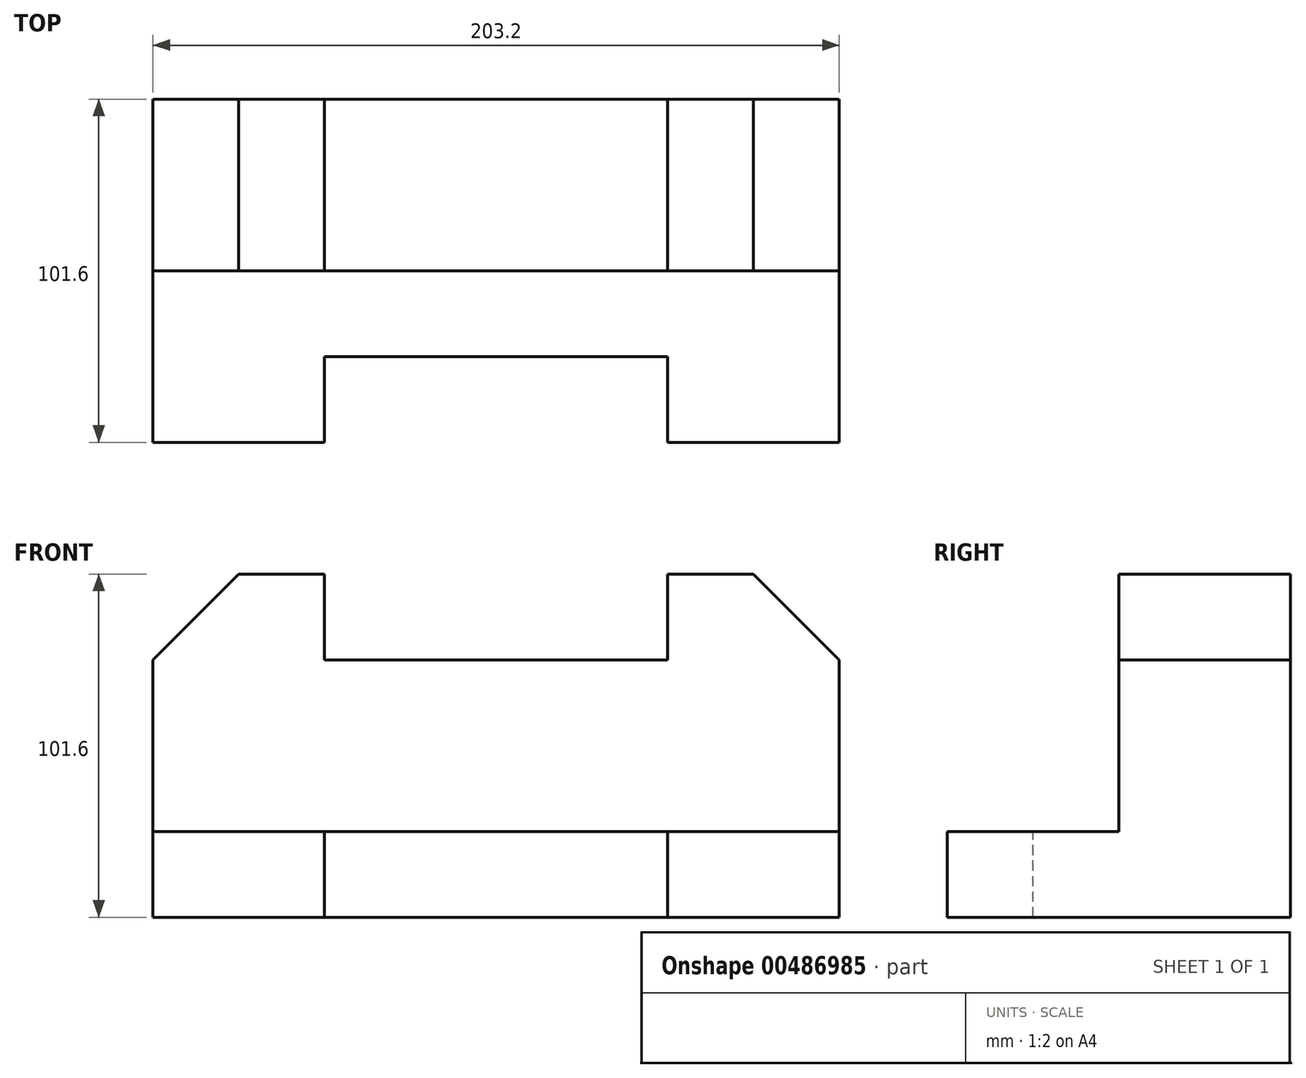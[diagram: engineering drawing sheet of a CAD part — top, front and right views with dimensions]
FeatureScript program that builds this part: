
annotation { "Feature Type Name" : "Feature", "Feature Type Description" : "" }
export const myFeature = defineFeature(function(context is Context, id is Id, definition is map)
    precondition{}
    {
        {
            var Q0;
            Q0=qCreatedBy(makeId("Front.planeOp"),FACE);
            var sketch = newSketch(context, id + "F0", { "sketchPlane" : qUnion([Q0])});
            skLineSegment(sketch, "E0.bottom", {"start": v(-85.33, 57.13) * mm, "end": v(117.87, 57.13) * mm});
            skLineSegment(sketch, "E0.top", {"start": v(-85.33, -44.47) * mm, "end": v(117.87, -44.47) * mm});
            skLineSegment(sketch, "E0.left", {"start": v(-85.33, 57.13) * mm, "end": v(-85.33, -44.47) * mm});
            skLineSegment(sketch, "E0.right", {"start": v(117.87, 57.13) * mm, "end": v(117.87, -44.47) * mm});
            skSolve(sketch);
        }
        {
            var Q0;
            Q0 = qSketchRegion(id + "F0", true);
            extrude(context, id + "F1", {"entities" : qUnion([Q0]), "depth" : 101.6 * mm});
        }
        {
            var Q0;
            Q0=makeQuery(id+"F1.opExtrude","CAP_FACE",FACE,{"disambiguationData":[OSD([sQuery(id+"F0.wireOp",EDGE,"E0.bottom"),sQuery(id+"F0.wireOp",EDGE,"E0.top"),sQuery(id+"F0.wireOp",EDGE,"E0.left"),sQuery(id+"F0.wireOp",EDGE,"E0.right")])],"isStart":false});
            var sketch = newSketch(context, id + "F2", { "sketchPlane" : qUnion([Q0])});
            skLineSegment(sketch, "E1", {"start": v(117.87, -44.47) * mm, "end": v(117.87, -19.07) * mm});
            skLineSegment(sketch, "E2", {"start": v(117.87, -19.07) * mm, "end": v(117.87, 57.13) * mm});
            skLineSegment(sketch, "E3", {"start": v(117.87, 57.13) * mm, "end": v(-85.33, 57.13) * mm});
            skLineSegment(sketch, "E4", {"start": v(-85.33, 57.13) * mm, "end": v(-85.33, -19.07) * mm});
            skLineSegment(sketch, "E5", {"start": v(-85.33, -19.07) * mm, "end": v(117.87, -19.07) * mm});
            skSolve(sketch);
        }
        {
            var Q0;
            Q0 = qSketchRegion(id + "F2", true);
            extrude(context, id + "F3", {"entities" : qUnion([Q0]), "operationType" : NewBodyOperationType.REMOVE, "oppositeDirection" : true, "depth" : 50.8 * mm});
        }
        {
            var Q0;
            Q0=makeQuery(id+"F1.opExtrude","CAP_FACE",FACE,{"disambiguationData":[OSD([sQuery(id+"F0.wireOp",EDGE,"E0.bottom"),sQuery(id+"F0.wireOp",EDGE,"E0.top"),sQuery(id+"F0.wireOp",EDGE,"E0.left"),sQuery(id+"F0.wireOp",EDGE,"E0.right")])],"isStart":false});
            var sketch = newSketch(context, id + "F4", { "sketchPlane" : qUnion([Q0])});
            skLineSegment(sketch, "E6", {"start": v(-85.33, -44.47) * mm, "end": v(-34.53, -44.47) * mm});
            skLineSegment(sketch, "E7", {"start": v(-34.53, -44.47) * mm, "end": v(67.07, -44.47) * mm});
            skLineSegment(sketch, "E8", {"start": v(67.07, -44.47) * mm, "end": v(117.87, -44.47) * mm});
            skLineSegment(sketch, "E9", {"start": v(67.07, -44.47) * mm, "end": v(67.07, -19.07) * mm});
            skLineSegment(sketch, "E10", {"start": v(67.07, -19.07) * mm, "end": v(-34.53, -19.07) * mm});
            skLineSegment(sketch, "E11", {"start": v(-34.53, -19.07) * mm, "end": v(-34.53, -44.47) * mm});
            skSolve(sketch);
        }
        {
            var Q0;
            Q0=makeQuery(id+"F4.imprint","IMPRINT",FACE,{"disambiguationData":[TD([[makeQuery(id+"F4.imprint","IMPRINT",EDGE,{"derivedFrom":sQuery(id+"F4.wireOp",EDGE,"E7")}),1.0]])]});
            extrude(context, id + "F5", {"entities" : qUnion([Q0]), "operationType" : NewBodyOperationType.REMOVE, "oppositeDirection" : true, "depth" : 25.4 * mm});
        }
        {
            var Q0;
            Q0=makeQuery(id+"F3.boolean.opBoolean","COPY",FACE,{"derivedFrom":makeQuery(id+"F3.opExtrude","CAP_FACE",FACE,{"disambiguationData":[OSD([sQuery(id+"F2.wireOp",EDGE,"E2"),sQuery(id+"F2.wireOp",EDGE,"E3"),sQuery(id+"F2.wireOp",EDGE,"E4"),sQuery(id+"F2.wireOp",EDGE,"E5")])],"isStart":false})});
            var sketch = newSketch(context, id + "F6", { "sketchPlane" : qUnion([Q0])});
            skLineSegment(sketch, "E12", {"start": v(-85.33, 57.13) * mm, "end": v(-34.53, 57.13) * mm});
            skLineSegment(sketch, "E13", {"start": v(-34.53, 57.13) * mm, "end": v(67.07, 57.13) * mm});
            skLineSegment(sketch, "E14", {"start": v(67.07, 57.13) * mm, "end": v(117.87, 57.13) * mm});
            skLineSegment(sketch, "E15", {"start": v(-34.53, 57.13) * mm, "end": v(-34.53, 31.73) * mm});
            skLineSegment(sketch, "E16", {"start": v(-34.53, 31.73) * mm, "end": v(67.07, 31.73) * mm});
            skLineSegment(sketch, "E17", {"start": v(67.07, 31.73) * mm, "end": v(67.07, 57.13) * mm});
            skSolve(sketch);
        }
        {
            var Q0;
            Q0=makeQuery(id+"F6.imprint","IMPRINT",FACE,{"disambiguationData":[TD([[makeQuery(id+"F6.imprint","IMPRINT",EDGE,{"derivedFrom":sQuery(id+"F6.wireOp",EDGE,"E13")}),-1.0]])]});
            extrude(context, id + "F7", {"entities" : qUnion([Q0]), "operationType" : NewBodyOperationType.REMOVE, "oppositeDirection" : true, "depth" : 50.8 * mm});
        }
        {
            var Q0;
            Q0=makeQuery(id+"F3.boolean.opBoolean","COPY",FACE,{"derivedFrom":makeQuery(id+"F3.opExtrude","CAP_FACE",FACE,{"disambiguationData":[OSD([sQuery(id+"F2.wireOp",EDGE,"E2"),sQuery(id+"F2.wireOp",EDGE,"E3"),sQuery(id+"F2.wireOp",EDGE,"E4"),sQuery(id+"F2.wireOp",EDGE,"E5")])],"isStart":false})});
            var sketch = newSketch(context, id + "F8", { "sketchPlane" : qUnion([Q0])});
            skLineSegment(sketch, "E18", {"start": v(117.87, 31.73) * mm, "end": v(117.87, 57.13) * mm});
            skLineSegment(sketch, "E19", {"start": v(117.87, 57.13) * mm, "end": v(92.47, 57.13) * mm});
            skLineSegment(sketch, "E20", {"start": v(92.47, 57.13) * mm, "end": v(117.87, 31.73) * mm});
            skSolve(sketch);
        }
        {
            var Q0;
            Q0=makeQuery(id+"F8.imprint","IMPRINT",FACE,{"disambiguationData":[TD([[makeQuery(id+"F8.imprint","IMPRINT",EDGE,{"derivedFrom":sQuery(id+"F8.wireOp",EDGE,"E18")}),-1.0]])]});
            extrude(context, id + "F9", {"entities" : qUnion([Q0]), "operationType" : NewBodyOperationType.REMOVE, "oppositeDirection" : true, "depth" : 50.8 * mm});
        }
        {
            var Q0;
            Q0=makeQuery(id+"F3.boolean.opBoolean","COPY",FACE,{"derivedFrom":makeQuery(id+"F3.opExtrude","CAP_FACE",FACE,{"disambiguationData":[OSD([sQuery(id+"F2.wireOp",EDGE,"E2"),sQuery(id+"F2.wireOp",EDGE,"E3"),sQuery(id+"F2.wireOp",EDGE,"E4"),sQuery(id+"F2.wireOp",EDGE,"E5")])],"isStart":false})});
            var sketch = newSketch(context, id + "F10", { "sketchPlane" : qUnion([Q0])});
            skLineSegment(sketch, "E21", {"start": v(-85.33, 31.73) * mm, "end": v(-85.33, 57.13) * mm});
            skLineSegment(sketch, "E22", {"start": v(-85.33, 57.13) * mm, "end": v(-59.93, 57.13) * mm});
            skLineSegment(sketch, "E23", {"start": v(-59.93, 57.13) * mm, "end": v(-85.33, 31.73) * mm});
            skSolve(sketch);
        }
        {
            var Q0;
            Q0=makeQuery(id+"F10.imprint","IMPRINT",FACE,{"disambiguationData":[TD([[makeQuery(id+"F10.imprint","IMPRINT",EDGE,{"derivedFrom":sQuery(id+"F10.wireOp",EDGE,"E21")}),1.0]])]});
            extrude(context, id + "F11", {"entities" : qUnion([Q0]), "operationType" : NewBodyOperationType.REMOVE, "oppositeDirection" : true, "depth" : 50.8 * mm});
        }
    });
